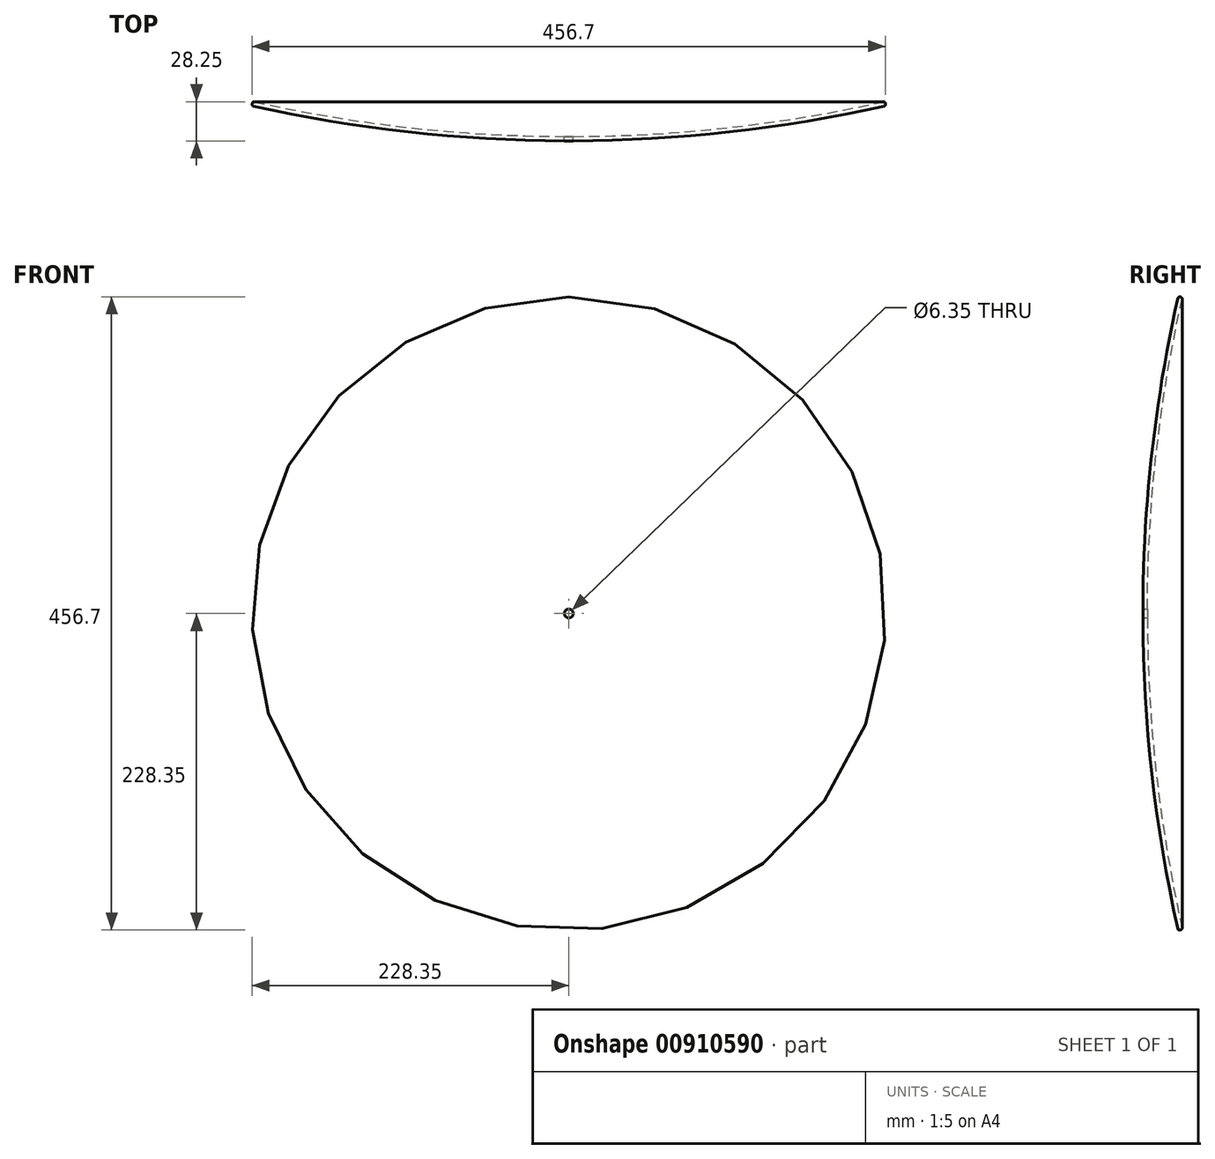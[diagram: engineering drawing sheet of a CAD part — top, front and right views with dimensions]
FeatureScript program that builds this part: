
annotation { "Feature Type Name" : "Feature", "Feature Type Description" : "" }
export const myFeature = defineFeature(function(context is Context, id is Id, definition is map)
    precondition{}
    {
        {
            var Q0;
            Q0=qCreatedBy(makeId("Right.planeOp"),FACE);
            var sketch = newSketch(context, id + "F0", { "sketchPlane" : qUnion([Q0])});
            skLineSegment(sketch, "E0", {"start": v(0, 228.6) * mm, "end": v(0, 0) * mm, "construction": true});
            skArc(sketch, "E1", {"start": v(-0.28, 227.36) * mm, "mid": v(-18.92, 115.95) * mm, "end": v(-25.4, 3.18) * mm});
            skLineSegment(sketch, "E2", {"start": v(0, 0) * mm, "end": v(-25.4, 0) * mm, "construction": true});
            skArc(sketch, "E3.0", {"start": v(2.82, 226.67) * mm, "mid": v(-15.77, 115.6) * mm, "end": v(-22.22, 3.17) * mm});
            skLineSegment(sketch, "E4", {"start": v(1.24, 228.32) * mm, "end": v(1.86, 228.18) * mm});
            skLineSegment(sketch, "E5", {"start": v(-6.63, 184.66) * mm, "end": v(3.1, 227.9) * mm, "construction": true});
            skLineSegment(sketch, "E6", {"start": v(-25.4, 3.17) * mm, "end": v(-22.22, 3.17) * mm});
            skPoint(sketch, "E7.visualSharp", {"position": v(3.1, 227.9) * mm});
            skArc(sketch, "E7.filletArc", {"start": v(2.82, 226.67) * mm, "mid": v(2.65, 227.62) * mm, "end": v(1.86, 228.18) * mm});
            skPoint(sketch, "E8.visualSharp", {"position": v(0, 228.6) * mm});
            skArc(sketch, "E8.filletArc", {"start": v(1.24, 228.32) * mm, "mid": v(0.28, 228.15) * mm, "end": v(-0.28, 227.36) * mm});
            skSolve(sketch);
        }
        {
            var Q0;
            Q0 = qSketchRegion(id + "F0", true);
            var Q1;
            Q1=sQuery(id+"F0.wireOp",EDGE,"E2");
            revolve(context, id + "F1", {"surfaceOperationType" : NewSurfaceOperationType.NEW, "entities" : qUnion([Q0]), "axis" : qUnion([Q1]), "revolveType" : RevolveType.FULL});
        }
    });
